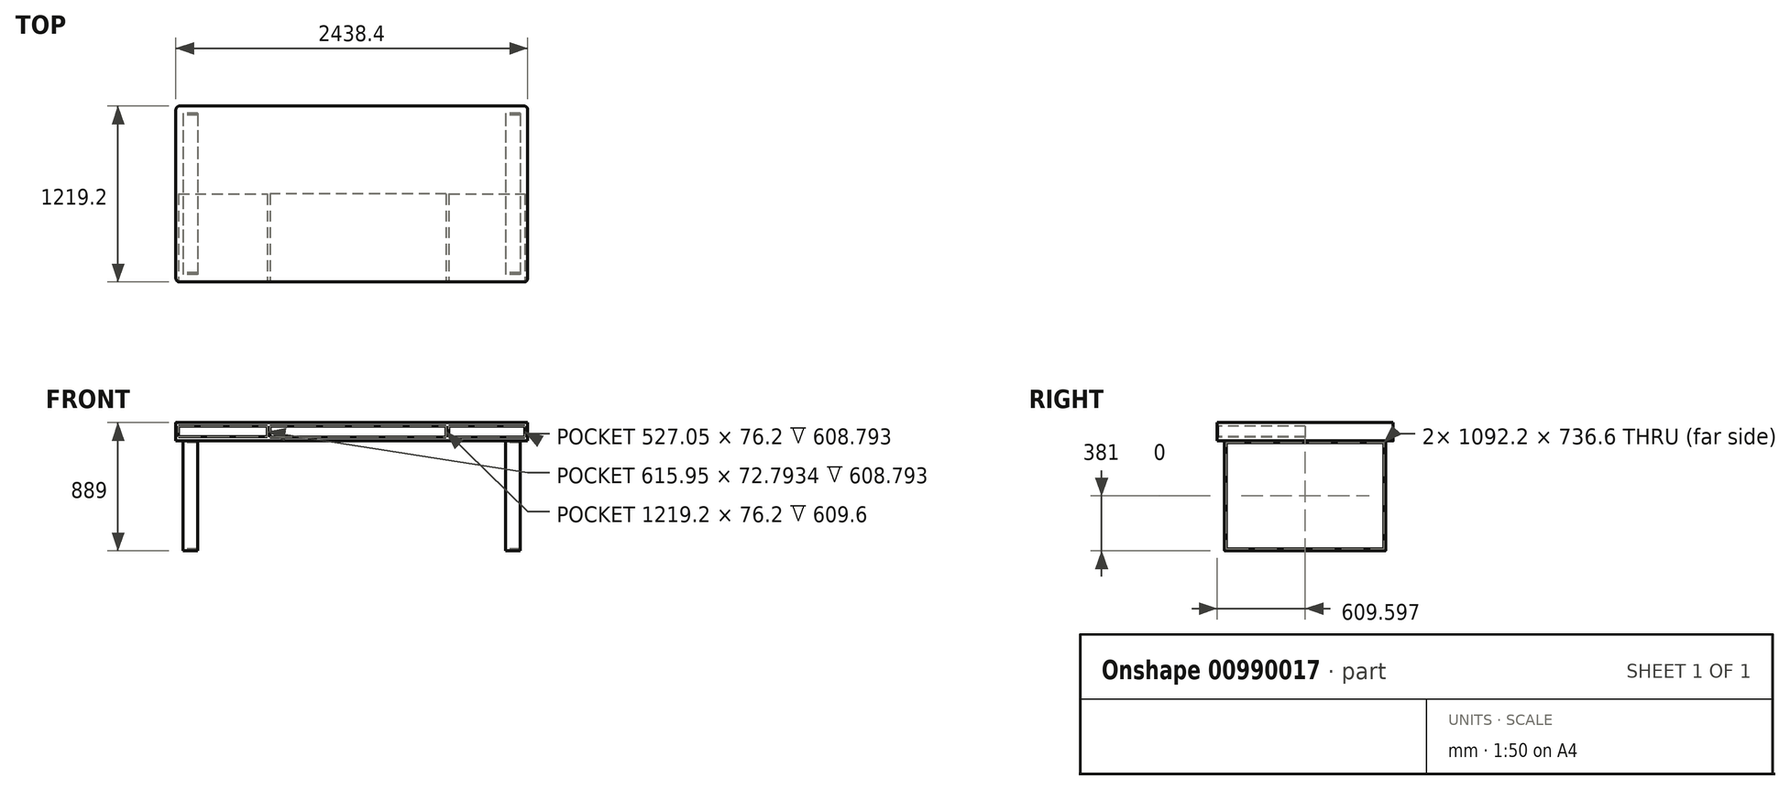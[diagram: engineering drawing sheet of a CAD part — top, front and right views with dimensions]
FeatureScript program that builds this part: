
annotation { "Feature Type Name" : "Feature", "Feature Type Description" : "" }
export const myFeature = defineFeature(function(context is Context, id is Id, definition is map)
    precondition{}
    {
        {
            var Q0;
            Q0=qCreatedBy(makeId("Top.planeOp"),FACE);
            var sketch = newSketch(context, id + "F0", { "sketchPlane" : qUnion([Q0])});
            skLineSegment(sketch, "E0.bottom", {"start": v(-744.03, 834.1) * mm, "end": v(1694.37, 834.1) * mm});
            skLineSegment(sketch, "E0.top", {"start": v(-744.03, -385.1) * mm, "end": v(1694.37, -385.1) * mm});
            skLineSegment(sketch, "E0.left", {"start": v(-744.03, 834.1) * mm, "end": v(-744.03, -385.1) * mm});
            skLineSegment(sketch, "E0.right", {"start": v(1694.37, 834.1) * mm, "end": v(1694.37, -385.1) * mm});
            skSolve(sketch);
        }
        {
            var Q0;
            Q0=makeQuery(id+"F0.imprint","IMPRINT",FACE,{"disambiguationData":[TD([[makeQuery(id+"F0.imprint","IMPRINT",EDGE,{"derivedFrom":sQuery(id+"F0.wireOp",EDGE,"E0.bottom")}),-1.0]])]});
            extrude(context, id + "F1", {"entities" : qUnion([Q0]), "depth" : 127 * mm, "offsetDistance" : 25.4 * mm});
        }
        {
            var Q0;
            Q0=makeQuery(id+"F1.opExtrude","CAP_FACE",FACE,{"disambiguationData":[OSD([sQuery(id+"F0.wireOp",EDGE,"E0.bottom"),sQuery(id+"F0.wireOp",EDGE,"E0.top"),sQuery(id+"F0.wireOp",EDGE,"E0.left"),sQuery(id+"F0.wireOp",EDGE,"E0.right")])],"isStart":true});
            var sketch = newSketch(context, id + "F2", { "sketchPlane" : qUnion([Q0])});
            skLineSegment(sketch, "E1.bottom", {"start": v(1643.57, -783.3) * mm, "end": v(1541.97, -783.3) * mm});
            skLineSegment(sketch, "E1.top", {"start": v(1643.57, 334.3) * mm, "end": v(1541.97, 334.3) * mm});
            skLineSegment(sketch, "E1.left", {"start": v(1643.57, -783.3) * mm, "end": v(1643.57, 334.3) * mm});
            skLineSegment(sketch, "E1.right", {"start": v(1541.97, -783.3) * mm, "end": v(1541.97, 334.3) * mm});
            skSolve(sketch);
        }
        {
            var Q0;
            Q0 = qSketchRegion(id + "F2", true);
            extrude(context, id + "F3", {"entities" : qUnion([Q0]), "depth" : 762 * mm, "offsetDistance" : 25.4 * mm});
        }
        {
            var Q0;
            Q0=makeQuery(id+"F3.opExtrude","SWEPT_FACE",FACE,{"disambiguationData":[OSD([sQuery(id+"F2.wireOp",EDGE,"E1.left")])]});
            var Q1;
            Q1=makeQuery(id+"F3.opExtrude","SWEPT_FACE",FACE,{"disambiguationData":[OSD([sQuery(id+"F2.wireOp",EDGE,"E1.right")])]});
            shell(context, id + "F4", {"entities" : qUnion([Q0, Q1]), "thickness" : 12.7 * mm});
        }
        {
            var Q0;
            Q0=makeQuery(id+"F3.opExtrude","SWEPT_BODY",BODY,{"disambiguationData":[OSD([sQuery(id+"F2.wireOp",EDGE,"E1.bottom"),sQuery(id+"F2.wireOp",EDGE,"E1.top"),sQuery(id+"F2.wireOp",EDGE,"E1.left"),sQuery(id+"F2.wireOp",EDGE,"E1.right")])]});
            transform(context, id + "F5", {"entities" : qUnion([Q0]), "transformType" : TransformType.TRANSLATION_3D, "dx" : -2235.2 * mm, "dy" : 0 * mm, "dz" : 0 * mm, "makeCopy" : true});
        }
        {
            var Q0;
            Q0=makeQuery(id+"F3.opExtrude","CAP_EDGE",EDGE,{"disambiguationData":[OSD([sQuery(id+"F2.wireOp",EDGE,"E1.bottom")])],"isStart":false});
            var Q1;
            Q1=makeQuery(id+"F3.opExtrude","CAP_EDGE",EDGE,{"disambiguationData":[OSD([sQuery(id+"F2.wireOp",EDGE,"E1.top")])],"isStart":false});
            var Q2;
            Q2=makeQuery(id+"F5.opPattern","COPY",EDGE,{"derivedFrom":makeQuery(id+"F3.opExtrude","CAP_EDGE",EDGE,{"disambiguationData":[OSD([sQuery(id+"F2.wireOp",EDGE,"E1.top")])],"isStart":false}),"instanceName":"1"});
            var Q3;
            Q3=makeQuery(id+"F5.opPattern","COPY",EDGE,{"derivedFrom":makeQuery(id+"F3.opExtrude","CAP_EDGE",EDGE,{"disambiguationData":[OSD([sQuery(id+"F2.wireOp",EDGE,"E1.bottom")])],"isStart":false}),"instanceName":"1"});
            fillet(context, id + "F6", {"entities" : qUnion([Q0, Q1, Q2, Q3]), "radius" : 5.08 * mm, "tangentPropagation" : true, "allowEdgeOverflow" : false});
        }
        {
            var Q0;
            Q0=makeQuery(id+"F1.opExtrude","SWEPT_EDGE",EDGE,{"disambiguationData":[OSD([sQuery(id+"F0.wireOp",EDGE,"E0.bottom"),sQuery(id+"F0.wireOp",EDGE,"E0.right")])]});
            var Q1;
            Q1=makeQuery(id+"F1.opExtrude","SWEPT_EDGE",EDGE,{"disambiguationData":[OSD([sQuery(id+"F0.wireOp",EDGE,"E0.top"),sQuery(id+"F0.wireOp",EDGE,"E0.right")])]});
            var Q2;
            Q2=makeQuery(id+"F1.opExtrude","SWEPT_EDGE",EDGE,{"disambiguationData":[OSD([sQuery(id+"F0.wireOp",EDGE,"E0.bottom"),sQuery(id+"F0.wireOp",EDGE,"E0.left")])]});
            var Q3;
            Q3=makeQuery(id+"F1.opExtrude","SWEPT_EDGE",EDGE,{"disambiguationData":[OSD([sQuery(id+"F0.wireOp",EDGE,"E0.top"),sQuery(id+"F0.wireOp",EDGE,"E0.left")])]});
            fillet(context, id + "F7", {"entities" : qUnion([Q0, Q1, Q2, Q3]), "radius" : 25.4 * mm, "tangentPropagation" : true, "allowEdgeOverflow" : false});
        }
        {
            var Q0;
            Q0=makeQuery(id+"F1.opExtrude","SWEPT_FACE",FACE,{"disambiguationData":[OSD([sQuery(id+"F0.wireOp",EDGE,"E0.top")])]});
            var sketch = newSketch(context, id + "F8", { "sketchPlane" : qUnion([Q0])});
            skLineSegment(sketch, "E2.bottom", {"start": v(1148.27, 101.6) * mm, "end": v(1675.32, 101.6) * mm});
            skLineSegment(sketch, "E2.top", {"start": v(1148.27, 25.4) * mm, "end": v(1675.32, 25.4) * mm});
            skLineSegment(sketch, "E2.left", {"start": v(1148.27, 101.6) * mm, "end": v(1148.27, 25.4) * mm});
            skLineSegment(sketch, "E2.right", {"start": v(1675.32, 101.6) * mm, "end": v(1675.32, 25.4) * mm});
            skLineSegment(sketch, "E3.bottom", {"start": v(1129.22, 101.6) * mm, "end": v(-89.98, 101.6) * mm});
            skLineSegment(sketch, "E3.top", {"start": v(1129.22, 25.4) * mm, "end": v(-89.98, 25.4) * mm});
            skLineSegment(sketch, "E3.left", {"start": v(1129.22, 101.6) * mm, "end": v(1129.22, 25.4) * mm});
            skLineSegment(sketch, "E3.right", {"start": v(-89.98, 101.6) * mm, "end": v(-89.98, 25.4) * mm});
            skLineSegment(sketch, "E4.bottom", {"start": v(-724.98, 101.5) * mm, "end": v(-109.03, 101.5) * mm});
            skLineSegment(sketch, "E4.top", {"start": v(-724.98, 28.7) * mm, "end": v(-109.03, 28.7) * mm});
            skLineSegment(sketch, "E4.left", {"start": v(-724.98, 101.5) * mm, "end": v(-724.98, 28.7) * mm});
            skLineSegment(sketch, "E4.right", {"start": v(-109.03, 101.5) * mm, "end": v(-109.03, 28.7) * mm});
            skSolve(sketch);
        }
        {
            var Q0;
            Q0 = qSketchRegion(id + "F8", true);
            extrude(context, id + "F9", {"entities" : qUnion([Q0]), "operationType" : NewBodyOperationType.REMOVE, "oppositeDirection" : true, "depth" : 609.6 * mm, "offsetDistance" : 25.4 * mm});
        }
        {
            var Q0;
            Q0=makeQuery(id+"F1.opExtrude","CAP_FACE",FACE,{"disambiguationData":[OSD([sQuery(id+"F0.wireOp",EDGE,"E0.bottom"),sQuery(id+"F0.wireOp",EDGE,"E0.top"),sQuery(id+"F0.wireOp",EDGE,"E0.left"),sQuery(id+"F0.wireOp",EDGE,"E0.right")])],"isStart":false});
            var sketch = newSketch(context, id + "F10", { "sketchPlane" : qUnion([Q0])});
            skCircle(sketch, "E5", {"center": v(430.26, 755.67) * mm, "radius": 44.67 * mm});
            skSolve(sketch);
        }
    });
